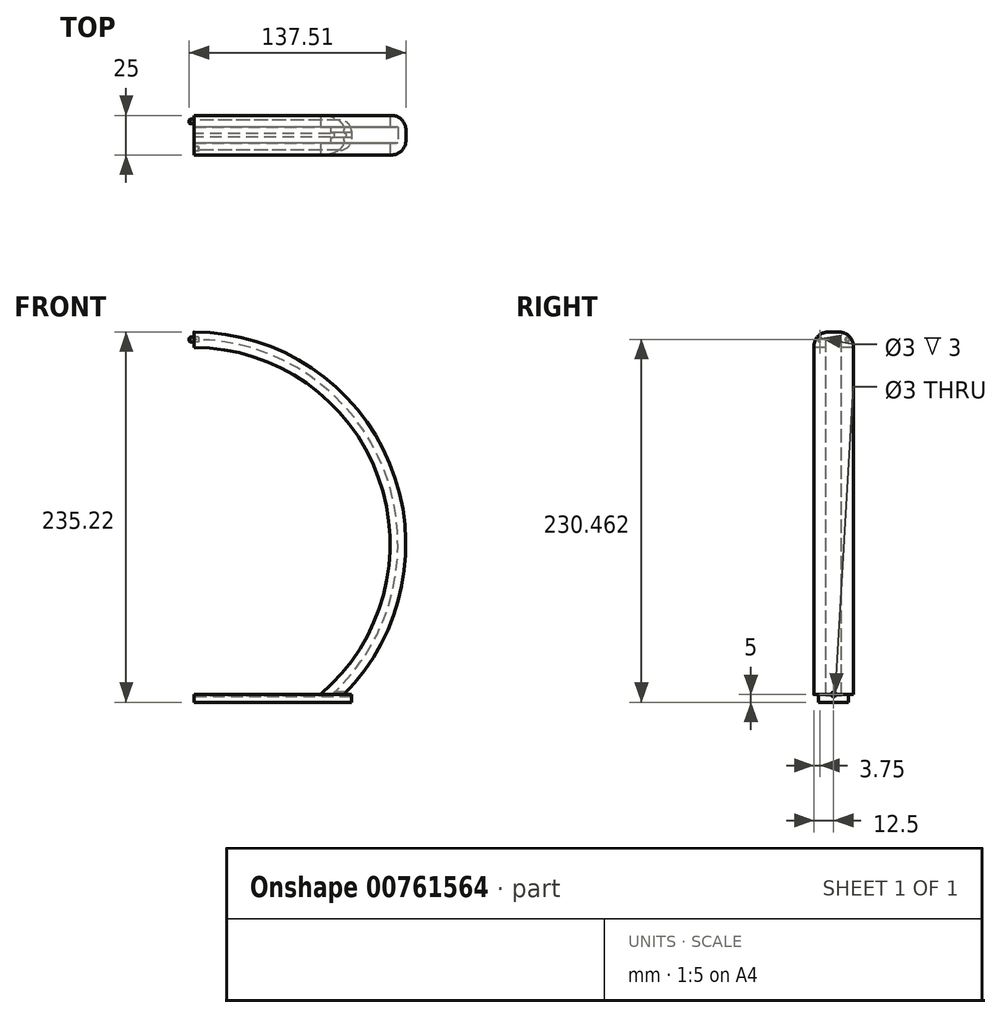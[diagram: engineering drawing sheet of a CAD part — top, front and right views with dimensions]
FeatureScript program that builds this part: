
annotation { "Feature Type Name" : "Feature", "Feature Type Description" : "" }
export const myFeature = defineFeature(function(context is Context, id is Id, definition is map)
    precondition{}
    {
        {
            var Q0;
            Q0=qCreatedBy(makeId("Front.planeOp"),FACE);
            var sketch = newSketch(context, id + "F0", { "sketchPlane" : qUnion([Q0])});
            skLineSegment(sketch, "E0", {"start": v(-96.18, 0) * mm, "end": v(95.2, 0) * mm});
            skArc(sketch, "E1", {"start": v(95.2, 0) * mm, "mid": v(-0.49, 230.22) * mm, "end": v(-96.18, 0) * mm});
            skSolve(sketch);
        }
        {
            var Q0;
            Q0=qSketchRegion(id+"F0",true);
            extrude(context, id + "F1", {"entities" : qUnion([Q0]), "endBound" : BoundingType.SYMMETRIC, "depth" : 25 * mm, "offsetDistance" : 25 * mm});
        }
        {
            var Q0;
            Q0=makeQuery(id+"F1.opExtrude","CAP_FACE",FACE,{"disambiguationData":[OSD([sQuery(id+"F0.wireOp",EDGE,"E0"),sQuery(id+"F0.wireOp",EDGE,"E1")])],"isStart":false});
            var sketch = newSketch(context, id + "F2", { "sketchPlane" : qUnion([Q0])});
            skLineSegment(sketch, "E2", {"start": v(-96.18, 0) * mm, "end": v(-81.18, 0) * mm});
            skLineSegment(sketch, "E3", {"start": v(95.2, 0) * mm, "end": v(80.2, 0) * mm});
            skArc(sketch, "E4", {"start": v(80.2, 0) * mm, "mid": v(-0.49, 220.46) * mm, "end": v(-81.18, 0) * mm});
            skSolve(sketch);
        }
        {
            var Q0;
            {var subQ0=sQuery(id+"F2.wireOp",EDGE,"E4");Q0=makeQuery(id+"F2.imprint","IMPRINT",FACE,{"disambiguationData":[TD([[makeQuery(id+"F2.imprint","IMPRINT",EDGE,{"derivedFrom":subQ0}),1.0]])]});}
            extrude(context, id + "F3", {"entities" : qUnion([Q0]), "operationType" : NewBodyOperationType.REMOVE, "endBound" : BoundingType.SYMMETRIC, "oppositeDirection" : true, "depth" : 290 * mm, "offsetDistance" : 25 * mm});
        }
        {
            var Q0;
            Q0=qCreatedBy(makeId("Top.planeOp"),FACE);
            var sketch = newSketch(context, id + "F4", { "sketchPlane" : qUnion([Q0])});
            skLineSegment(sketch, "E5.bottom", {"start": v(100, 9.5) * mm, "end": v(-100, 9.5) * mm});
            skLineSegment(sketch, "E5.top", {"start": v(100, -9.5) * mm, "end": v(-100, -9.5) * mm});
            skLineSegment(sketch, "E5.left", {"start": v(100, 9.5) * mm, "end": v(100, -9.5) * mm});
            skLineSegment(sketch, "E5.right", {"start": v(-100, 9.5) * mm, "end": v(-100, -9.5) * mm});
            skPoint(sketch, "E5.middle", {"position": v(0, 0) * mm});
            skSolve(sketch);
        }
        {
            var Q0;
            Q0=qSketchRegion(id+"F4",true);
            extrude(context, id + "F5", {"entities" : qUnion([Q0]), "operationType" : NewBodyOperationType.ADD, "oppositeDirection" : true, "depth" : 5 * mm, "offsetDistance" : 25 * mm});
        }
        {
            var Q0;
            Q0=qCreatedBy(makeId("Front.planeOp"),FACE);
            var sketch = newSketch(context, id + "F6", { "sketchPlane" : qUnion([Q0])});
            skLineSegment(sketch, "E6", {"start": v(-87.56, -1.07) * mm, "end": v(86.58, -1.07) * mm});
            skArc(sketch, "E7.0", {"start": v(86.58, -1.07) * mm, "mid": v(-0.49, 225.46) * mm, "end": v(-87.56, -1.07) * mm});
            skSolve(sketch);
        }
        {
            var Q0;
            Q0=qSketchRegion(id+"F6",true);
            extrude(context, id + "F7", {"entities" : qUnion([Q0]), "operationType" : NewBodyOperationType.REMOVE, "endBound" : BoundingType.SYMMETRIC, "oppositeDirection" : true, "depth" : 10 * mm});
        }
        {
            var Q0;
            Q0=qCreatedBy(makeId("Right.planeOp"),FACE);
            var sketch = newSketch(context, id + "F8", { "sketchPlane" : qUnion([Q0])});
            skCircle(sketch, "E8", {"center": v(0, 0) * mm, "radius": 1 * mm});
            skSolve(sketch);
        }
        {
            var Q0;
            Q0=qSketchRegion(id+"F8",true);
            extrude(context, id + "F9", {"entities" : qUnion([Q0]), "operationType" : NewBodyOperationType.REMOVE, "endBound" : BoundingType.THROUGH_ALL, "oppositeDirection" : true, "depth" : 25 * mm});
        }
        {
            var Q0;
            Q0=makeQuery(id+"F5.opExtrude","CAP_FACE",FACE,{"disambiguationData":[OSD([sQuery(id+"F4.wireOp",EDGE,"E5.bottom"),sQuery(id+"F4.wireOp",EDGE,"E5.top"),sQuery(id+"F4.wireOp",EDGE,"E5.left"),sQuery(id+"F4.wireOp",EDGE,"E5.right")])],"isStart":false});
            var sketch = newSketch(context, id + "F10", { "sketchPlane" : qUnion([Q0])});
            skLineSegment(sketch, "E9", {"start": v(0, 0) * mm, "end": v(43.09, 0) * mm});
            skLineSegment(sketch, "E10", {"start": v(0, 0) * mm, "end": v(-27.56, 0) * mm});
            skCircle(sketch, "E11", {"center": v(-27.56, 0) * mm, "radius": 2.5 * mm});
            skCircle(sketch, "E12", {"center": v(43.09, 0) * mm, "radius": 2.5 * mm});
            skSolve(sketch);
        }
        {
            var Q0;
            Q0=makeQuery(id+"F1.opExtrude","CAP_EDGE",EDGE,{"disambiguationData":[OSD([sQuery(id+"F0.wireOp",EDGE,"E1")])],"isStart":false});
            var Q1;
            Q1=makeQuery(id+"F1.opExtrude","CAP_EDGE",EDGE,{"disambiguationData":[OSD([sQuery(id+"F0.wireOp",EDGE,"E1")])],"isStart":true});
            fillet(context, id + "F11", {"entities" : qUnion([Q0, Q1]), "radius" : 9 * mm, "tangentPropagation" : true, "allowEdgeOverflow" : false});
        }
        {
            var Q0;
            Q0=qCreatedBy(makeId("Front.planeOp"),FACE);
            var sketch = newSketch(context, id + "F12", { "sketchPlane" : qUnion([Q0])});
            skLineSegment(sketch, "E13.bottom", {"start": v(0, -27.8) * mm, "end": v(-164.37, -27.8) * mm});
            skLineSegment(sketch, "E13.top", {"start": v(0, 271.3) * mm, "end": v(-164.37, 271.3) * mm});
            skLineSegment(sketch, "E13.left", {"start": v(0, -27.8) * mm, "end": v(0, 271.3) * mm});
            skLineSegment(sketch, "E13.right", {"start": v(-164.37, -27.8) * mm, "end": v(-164.37, 271.3) * mm});
            skSolve(sketch);
        }
        {
            var Q0;
            Q0=qSketchRegion(id+"F12",true);
            extrude(context, id + "F13", {"entities" : qUnion([Q0]), "operationType" : NewBodyOperationType.REMOVE, "endBound" : BoundingType.SYMMETRIC, "oppositeDirection" : true, "depth" : 30 * mm});
        }
        {
            var Q0;
            {var subQ2=sQuery(id+"F0.wireOp",EDGE,"E1");Q0=makeQuery(id+"F13.boolean.opBoolean","COPY",FACE,{"disambiguationData":[TD([makeQuery(id+"F1.opExtrude","SWEPT_FACE",FACE,{"disambiguationData":[OSD([subQ2])]})])],"derivedFrom":makeQuery(id+"F13.opExtrude","SWEPT_FACE",FACE,{"disambiguationData":[OSD([sQuery(id+"F12.wireOp",EDGE,"E13.left")])]})});}
            var sketch = newSketch(context, id + "F14", { "sketchPlane" : qUnion([Q0])});
            skCircle(sketch, "E14", {"center": v(-8.75, 225.46) * mm, "radius": 1.5 * mm});
            skPoint(sketch, "E14.centerSnap0", {"position": v(-8.75, 220.46) * mm});
            skPoint(sketch, "E15.centerSnap0", {"position": v(8.75, 220.46) * mm});
            skSolve(sketch);
        }
        {
            var Q0;
            Q0=makeQuery(id+"F14.imprint","IMPRINT",FACE,{"disambiguationData":[TD([[makeQuery(id+"F14.imprint","IMPRINT",EDGE,{"derivedFrom":sQuery(id+"F14.wireOp",EDGE,"E14")}),1.0]])]});
            extrude(context, id + "F15", {"entities" : qUnion([Q0]), "operationType" : NewBodyOperationType.ADD, "depth" : 3 * mm});
        }
        {
            var Q0;
            {var subQ2=sQuery(id+"F0.wireOp",EDGE,"E1");Q0=makeQuery(id+"F13.boolean.opBoolean","COPY",FACE,{"disambiguationData":[TD([makeQuery(id+"F1.opExtrude","SWEPT_FACE",FACE,{"disambiguationData":[OSD([subQ2])]})])],"derivedFrom":makeQuery(id+"F13.opExtrude","SWEPT_FACE",FACE,{"disambiguationData":[OSD([sQuery(id+"F12.wireOp",EDGE,"E13.left")])]})});}
            var sketch = newSketch(context, id + "F16", { "sketchPlane" : qUnion([Q0])});
            skCircle(sketch, "E16", {"center": v(8.75, 225.46) * mm, "radius": 1.5 * mm});
            skPoint(sketch, "E16.centerSnap0", {"position": v(8.75, 220.46) * mm});
            skSolve(sketch);
        }
        {
            var Q0;
            Q0=qSketchRegion(id+"F16",true);
            extrude(context, id + "F17", {"entities" : qUnion([Q0]), "operationType" : NewBodyOperationType.REMOVE, "oppositeDirection" : true, "depth" : 3 * mm});
        }
        {
            var Q0;
            Q0=makeQuery(id+"F15.opExtrude","CAP_EDGE",EDGE,{"disambiguationData":[OSD([sQuery(id+"F14.wireOp",EDGE,"E14")])],"isStart":false});
            chamfer(context, id + "F18", {"entities" : qUnion([Q0]), "width" : 0.5 * mm, "tangentPropagation" : true});
        }
        {
            var Q0;
            Q0=qCreatedBy(makeId("Right.planeOp"),FACE);
            var sketch = newSketch(context, id + "F19", { "sketchPlane" : qUnion([Q0])});
            skCircle(sketch, "E17", {"center": v(0, 0) * mm, "radius": 1.5 * mm});
            skSolve(sketch);
        }
        {
            var Q0;
            Q0=qSketchRegion(id+"F19",true);
            extrude(context, id + "F20", {"entities" : qUnion([Q0]), "operationType" : NewBodyOperationType.REMOVE, "endBound" : BoundingType.THROUGH_ALL, "depth" : 25 * mm});
        }
        {
            var Q0;
            Q0=makeQuery(id+"F5.opExtrude","SWEPT_EDGE",EDGE,{"disambiguationData":[OSD([sQuery(id+"F4.wireOp",EDGE,"E5.bottom"),sQuery(id+"F4.wireOp",EDGE,"E5.left")])]});
            var Q1;
            Q1=makeQuery(id+"F5.opExtrude","SWEPT_EDGE",EDGE,{"disambiguationData":[OSD([sQuery(id+"F4.wireOp",EDGE,"E5.top"),sQuery(id+"F4.wireOp",EDGE,"E5.left")])]});
            fillet(context, id + "F21", {"entities" : qUnion([Q0, Q1]), "radius" : 7 * mm, "tangentPropagation" : true, "allowEdgeOverflow" : false});
        }
    });
